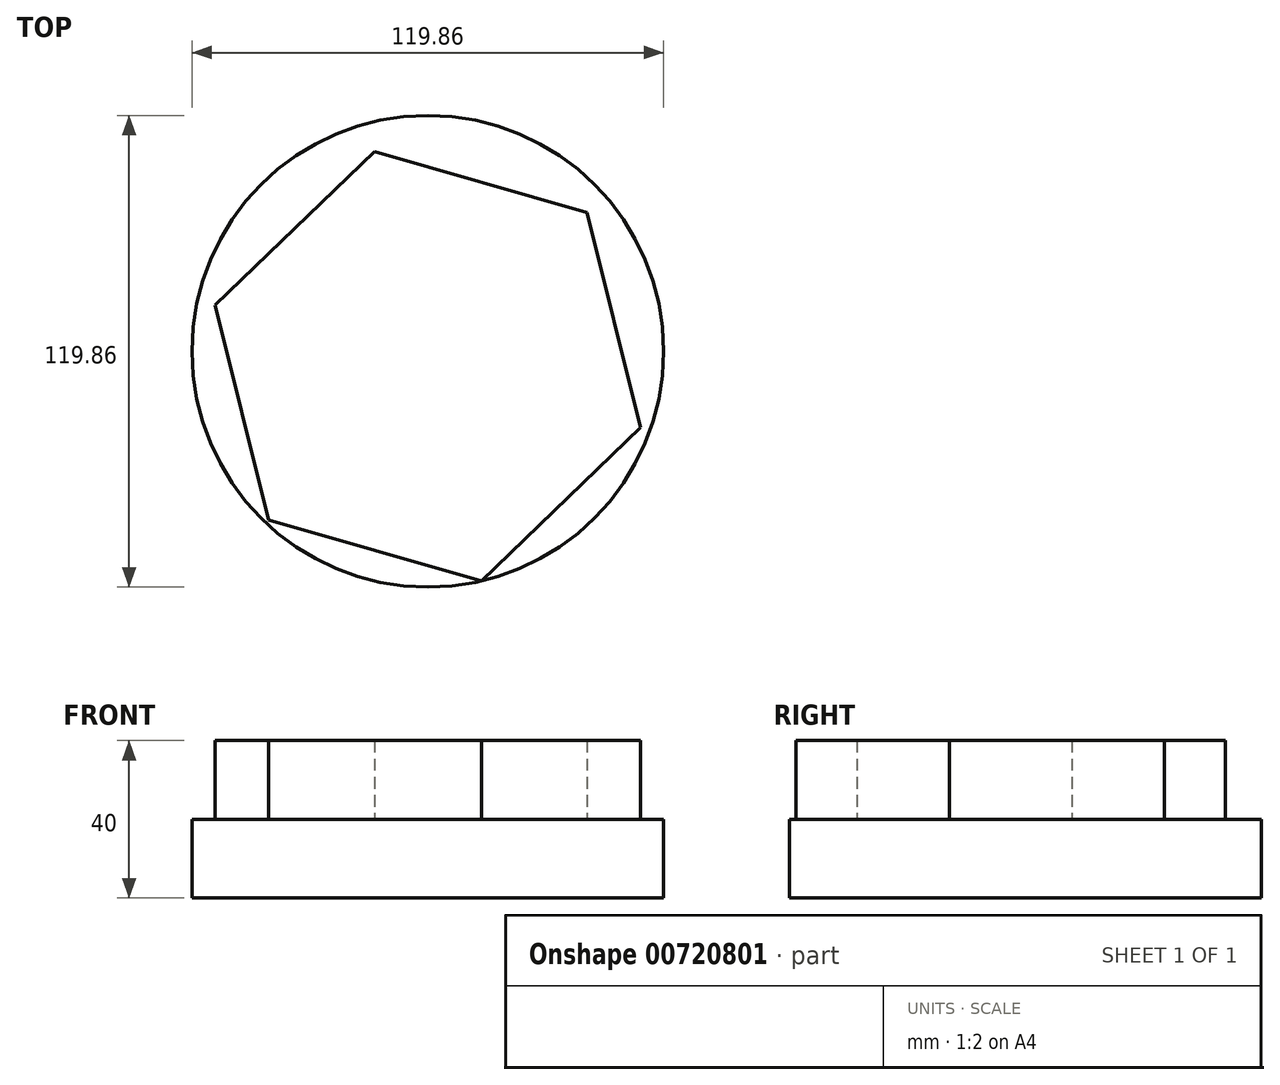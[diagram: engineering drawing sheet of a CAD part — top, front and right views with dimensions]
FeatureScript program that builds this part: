
annotation { "Feature Type Name" : "Feature", "Feature Type Description" : "" }
export const myFeature = defineFeature(function(context is Context, id is Id, definition is map)
    precondition{}
    {
        {
            var Q0;
            Q0=qCreatedBy(makeId("Top.planeOp"),FACE);
            var sketch = newSketch(context, id + "F0", { "sketchPlane" : qUnion([Q0])});
            skCircle(sketch, "E0", {"center": v(0, 0) * mm, "radius": 59.93 * mm});
            skSolve(sketch);
        }
        {
            var Q0;
            Q0 = qSketchRegion(id + "F0", true);
            extrude(context, id + "F1", {"entities" : qUnion([Q0]), "depth" : 20 * mm, "offsetDistance" : 25.4 * mm});
        }
        {
            var Q0;
            Q0=makeQuery(id+"F1.opExtrude","CAP_FACE",FACE,{"disambiguationData":[OSD([sQuery(id+"F0.wireOp",EDGE,"E0")])],"isStart":false});
            var sketch = newSketch(context, id + "F2", { "sketchPlane" : qUnion([Q0])});
            skCircle(sketch, "E1.cCircle", {"center": v(0, -3.8) * mm, "radius": 56.23 * mm, "construction": true});
            skLineSegment(sketch, "E1.0", {"start": v(13.6, -58.36) * mm, "end": v(-40.45, -42.86) * mm});
            skLineSegment(sketch, "E1.1", {"start": v(-40.45, -42.86) * mm, "end": v(-54.05, 11.7) * mm});
            skLineSegment(sketch, "E1.2", {"start": v(-54.05, 11.7) * mm, "end": v(-13.6, 50.76) * mm});
            skLineSegment(sketch, "E1.3", {"start": v(-13.6, 50.76) * mm, "end": v(40.45, 35.25) * mm});
            skLineSegment(sketch, "E1.4", {"start": v(40.45, 35.25) * mm, "end": v(54.05, -19.31) * mm});
            skLineSegment(sketch, "E1.5", {"start": v(54.05, -19.31) * mm, "end": v(13.6, -58.36) * mm});
            skSolve(sketch);
        }
        {
            var Q0;
            Q0=makeQuery(id+"F2.imprint","IMPRINT",FACE,{"disambiguationData":[TD([[makeQuery(id+"F2.imprint","IMPRINT",EDGE,{"derivedFrom":sQuery(id+"F2.wireOp",EDGE,"E1.0")}),-1.0]])]});
            extrude(context, id + "F3", {"entities" : qUnion([Q0]), "operationType" : NewBodyOperationType.ADD, "depth" : 20 * mm, "offsetDistance" : 25.4 * mm});
        }
    });
